# Revit family: Im-Beton-Kanalsystem_IBK_Verbindungselement_38_mm
name_source: partatom
category: Generic Models
revit_build: Autodesk Revit 2015 (Build: 20140606_1530(x64)
units: mm (PartAtom-declared; Revit-internal decimal feet)

## types (2) — shared parameters
Height = 38 mm  [stored 0.124672 ft]
Manufacturer = OBO Bettermann
Material = Steel, Galvanized
URL = http://www.obo-bettermann.com

## per-type parameters (varying)
| type | GTIN | Manufacturer Art. No. | Outer width | Width | Width 2 |
| IBVE 35038 | 4012196331857
4012196331857 | 7399896 | 428 mm  [stored 1.4042 ft] | 350 mm  [stored 1.14829 ft] | 357 mm  [stored 1.17126 ft] |
| IBVE 25038 | 4012196331833

4012196331833
4012196331833
4012196331789 | 7399890 | 328 mm  [stored 1.07612 ft] | 250 mm  [stored 0.82021 ft] | 257 mm  [stored 0.843176 ft] |

note: column(s) folded — value = type name in every type: Article Type

note: [stored X ft] marks values corroborated as IEEE doubles in the binary element streams (Revit-internal decimal feet)

## geometry (parser evidence)
native form markers: Sweep x2
no freeform markers — native parametric forms only
